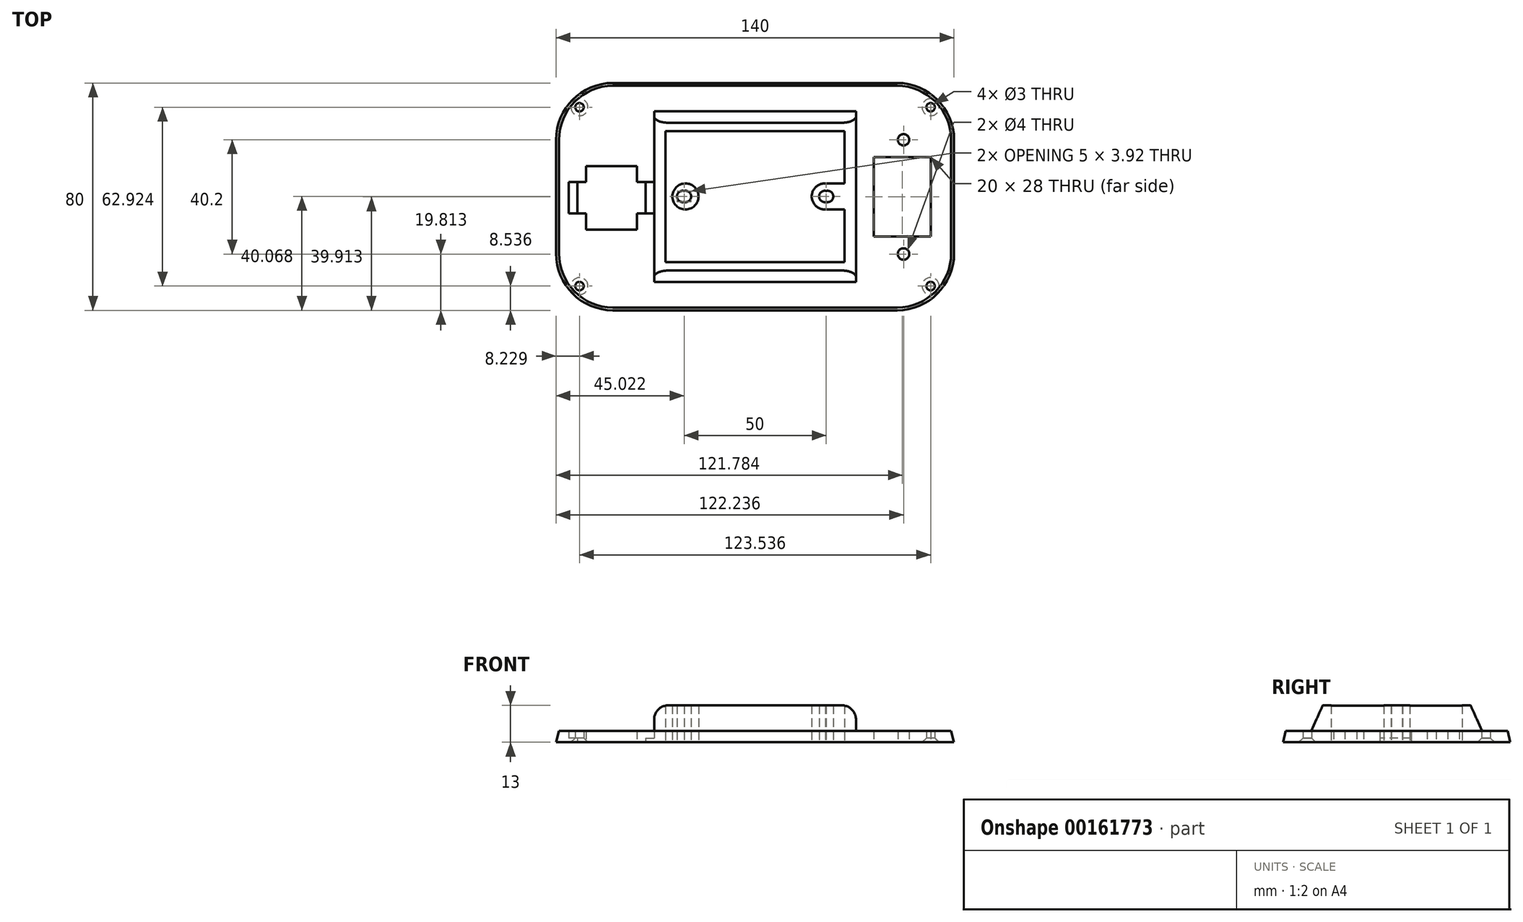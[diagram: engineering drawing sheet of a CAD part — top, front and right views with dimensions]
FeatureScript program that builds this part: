
annotation { "Feature Type Name" : "Feature", "Feature Type Description" : "" }
export const myFeature = defineFeature(function(context is Context, id is Id, definition is map)
    precondition{}
    {
        {
            var Q0;
            Q0=qCreatedBy(makeId("Top.planeOp"),FACE);
            var sketch = newSketch(context, id + "F0", { "sketchPlane" : qUnion([Q0])});
            skPoint(sketch, "E0.middle", {"position": v(7.13, 0.12) * mm});
            skLineSegment(sketch, "E1.bottom", {"start": v(38.63, 23.12) * mm, "end": v(-24.37, 23.12) * mm});
            skLineSegment(sketch, "E1.top", {"start": v(38.63, -22.88) * mm, "end": v(-24.37, -22.88) * mm});
            skLineSegment(sketch, "E1.left", {"start": v(38.63, 23.12) * mm, "end": v(38.63, -22.88) * mm});
            skLineSegment(sketch, "E1.right", {"start": v(-24.37, 23.12) * mm, "end": v(-24.37, -22.88) * mm});
            skCircle(sketch, "E2", {"center": v(31.65, 0.19) * mm, "radius": 2 * mm});
            skPoint(sketch, "E3.middle", {"position": v(32.65, 0.19) * mm});
            skPoint(sketch, "E4.middle", {"position": v(-18.35, 0.19) * mm});
            skCircle(sketch, "E5", {"center": v(-17.35, 0.19) * mm, "radius": 2 * mm});
            skCircle(sketch, "E6", {"center": v(59.37, 20.13) * mm, "radius": 2 * mm});
            skCircle(sketch, "E7", {"center": v(59.37, -20.07) * mm, "radius": 2 * mm});
            skPoint(sketch, "E8.middle", {"position": v(58.91, 0.03) * mm});
            skPoint(sketch, "E9.visualSharp", {"position": v(-62.87, 30.12) * mm});
            skPoint(sketch, "E10.visualSharp", {"position": v(77.13, 30.12) * mm});
            skPoint(sketch, "E11.visualSharp", {"position": v(77.13, -29.88) * mm});
            skPoint(sketch, "E12.visualSharp", {"position": v(-62.87, -29.88) * mm});
            skLineSegment(sketch, "E13.bottom", {"start": v(-34.39, -11.43) * mm, "end": v(-52.39, -11.43) * mm});
            skLineSegment(sketch, "E13.top", {"start": v(-34.39, 10.87) * mm, "end": v(-52.39, 10.87) * mm});
            skLineSegment(sketch, "E13.left", {"start": v(-34.39, -11.43) * mm, "end": v(-34.39, 10.87) * mm});
            skLineSegment(sketch, "E13.right", {"start": v(-52.39, -11.43) * mm, "end": v(-52.39, 10.87) * mm});
            skPoint(sketch, "E13.middle", {"position": v(-43.39, -0.28) * mm});
            skLineSegment(sketch, "E14.bottom", {"start": v(-55.39, 5.22) * mm, "end": v(-31.39, 5.22) * mm});
            skLineSegment(sketch, "E14.top", {"start": v(-55.39, -5.78) * mm, "end": v(-31.39, -5.78) * mm});
            skLineSegment(sketch, "E14.left", {"start": v(-55.39, 5.22) * mm, "end": v(-55.39, -5.78) * mm});
            skLineSegment(sketch, "E14.right", {"start": v(-31.39, 5.22) * mm, "end": v(-31.39, -5.78) * mm});
            skLineSegment(sketch, "E15.bottom", {"start": v(-28.39, 30.12) * mm, "end": v(42.64, 30.12) * mm});
            skLineSegment(sketch, "E15.top", {"start": v(-28.39, -29.88) * mm, "end": v(42.64, -29.88) * mm});
            skLineSegment(sketch, "E15.left", {"start": v(-28.39, 30.12) * mm, "end": v(-28.39, -29.88) * mm});
            skLineSegment(sketch, "E15.right", {"start": v(42.64, 30.12) * mm, "end": v(42.64, -29.88) * mm});
            skLineSegment(sketch, "E16.bottom", {"start": v(-31.39, 5.22) * mm, "end": v(-28.39, 5.22) * mm});
            skLineSegment(sketch, "E16.top", {"start": v(-31.39, -5.78) * mm, "end": v(-28.39, -5.78) * mm});
            skLineSegment(sketch, "E16.right", {"start": v(-28.39, 5.22) * mm, "end": v(-28.39, -5.78) * mm});
            skLineSegment(sketch, "E17.bottom", {"start": v(-55.39, 5.22) * mm, "end": v(-58.39, 5.22) * mm});
            skLineSegment(sketch, "E17.top", {"start": v(-55.39, -5.78) * mm, "end": v(-58.39, -5.78) * mm});
            skLineSegment(sketch, "E17.right", {"start": v(-58.39, 5.22) * mm, "end": v(-58.39, -5.78) * mm});
            skLineSegment(sketch, "E18.bottom", {"start": v(57.13, 40.12) * mm, "end": v(-42.87, 40.12) * mm});
            skLineSegment(sketch, "E18.top", {"start": v(57.13, -39.88) * mm, "end": v(-42.87, -39.88) * mm});
            skLineSegment(sketch, "E18.left", {"start": v(77.13, 20.12) * mm, "end": v(77.13, -19.88) * mm});
            skLineSegment(sketch, "E18.right", {"start": v(-62.87, 20.12) * mm, "end": v(-62.87, -19.88) * mm});
            skPoint(sketch, "E19.visualSharp", {"position": v(-62.87, 40.12) * mm});
            skArc(sketch, "E19.filletArc", {"start": v(-42.87, 40.12) * mm, "mid": v(-57.01, 34.26) * mm, "end": v(-62.87, 20.12) * mm});
            skPoint(sketch, "E20.visualSharp", {"position": v(77.13, 40.12) * mm});
            skArc(sketch, "E20.filletArc", {"start": v(77.13, 20.12) * mm, "mid": v(71.27, 34.26) * mm, "end": v(57.13, 40.12) * mm});
            skPoint(sketch, "E21.visualSharp", {"position": v(77.13, -39.88) * mm});
            skArc(sketch, "E21.filletArc", {"start": v(57.13, -39.88) * mm, "mid": v(71.27, -34.02) * mm, "end": v(77.13, -19.88) * mm});
            skPoint(sketch, "E22.visualSharp", {"position": v(-62.87, -39.88) * mm});
            skArc(sketch, "E22.filletArc", {"start": v(-62.87, -19.88) * mm, "mid": v(-57.01, -34.02) * mm, "end": v(-42.87, -39.88) * mm});
            skLineSegment(sketch, "E23.bottom", {"start": v(-42.87, 44.12) * mm, "end": v(57.13, 44.12) * mm});
            skLineSegment(sketch, "E23.top", {"start": v(-42.87, -43.88) * mm, "end": v(57.13, -43.88) * mm});
            skLineSegment(sketch, "E23.left", {"start": v(-66.87, 20.12) * mm, "end": v(-66.87, -19.88) * mm});
            skLineSegment(sketch, "E23.right", {"start": v(81.13, 20.12) * mm, "end": v(81.13, -19.88) * mm});
            skPoint(sketch, "E24.visualSharp", {"position": v(-66.87, 44.12) * mm});
            skArc(sketch, "E24.filletArc", {"start": v(-42.87, 44.12) * mm, "mid": v(-59.84, 37.09) * mm, "end": v(-66.87, 20.12) * mm});
            skPoint(sketch, "E25.visualSharp", {"position": v(81.13, 44.12) * mm});
            skArc(sketch, "E25.filletArc", {"start": v(81.13, 20.12) * mm, "mid": v(74.1, 37.09) * mm, "end": v(57.13, 44.12) * mm});
            skPoint(sketch, "E26.visualSharp", {"position": v(81.13, -43.88) * mm});
            skArc(sketch, "E26.filletArc", {"start": v(57.13, -43.88) * mm, "mid": v(74.1, -36.85) * mm, "end": v(81.13, -19.88) * mm});
            skPoint(sketch, "E27.visualSharp", {"position": v(-66.87, -43.88) * mm});
            skArc(sketch, "E27.filletArc", {"start": v(-66.87, -19.88) * mm, "mid": v(-59.84, -36.85) * mm, "end": v(-42.87, -43.88) * mm});
            skCircle(sketch, "E28", {"center": v(68.9, 31.58) * mm, "radius": 3.5 * mm});
            skCircle(sketch, "E29", {"center": v(68.9, 31.58) * mm, "radius": 1.5 * mm});
            skCircle(sketch, "E30", {"center": v(-54.64, 31.58) * mm, "radius": 3.5 * mm});
            skCircle(sketch, "E31", {"center": v(-54.64, 31.58) * mm, "radius": 1.5 * mm});
            skCircle(sketch, "E32", {"center": v(-54.64, -31.34) * mm, "radius": 3.5 * mm});
            skCircle(sketch, "E33", {"center": v(-54.64, -31.34) * mm, "radius": 1.5 * mm});
            skCircle(sketch, "E34", {"center": v(68.9, -31.34) * mm, "radius": 3.5 * mm});
            skCircle(sketch, "E35", {"center": v(68.9, -31.34) * mm, "radius": 1.5 * mm});
            skLineSegment(sketch, "E36.right", {"start": v(-24.37, 4.8) * mm, "end": v(-24.37, -4.4) * mm});
            skCircle(sketch, "E37", {"center": v(-17.35, 0.19) * mm, "radius": 4.6 * mm});
            skCircle(sketch, "E38", {"center": v(31.65, 0.19) * mm, "radius": 4.59 * mm});
            skLineSegment(sketch, "E39", {"start": v(31.92, 4.77) * mm, "end": v(38.65, 4.8) * mm});
            skLineSegment(sketch, "E40", {"start": v(31.64, -4.4) * mm, "end": v(38.65, -4.43) * mm});
            skLineSegment(sketch, "E41", {"start": v(-17.31, -4.4) * mm, "end": v(-24.37, -4.4) * mm});
            skLineSegment(sketch, "E42", {"start": v(-17.51, 4.78) * mm, "end": v(-24.37, 4.8) * mm});
            skLineSegment(sketch, "E43.bottom", {"start": v(68.91, 14.03) * mm, "end": v(48.91, 14.03) * mm});
            skLineSegment(sketch, "E43.top", {"start": v(68.91, -13.97) * mm, "end": v(48.91, -13.97) * mm});
            skLineSegment(sketch, "E43.left", {"start": v(68.91, 14.03) * mm, "end": v(68.91, -13.97) * mm});
            skLineSegment(sketch, "E43.right", {"start": v(48.91, 14.03) * mm, "end": v(48.91, -13.97) * mm});
            skCircle(sketch, "E44", {"center": v(-18.35, 0.19) * mm, "radius": 2 * mm});
            skCircle(sketch, "E45", {"center": v(32.65, 0.19) * mm, "radius": 2 * mm});
            skSolve(sketch);
        }
        {
            var Q0;
            Q0=makeQuery(id+"F0.imprint","IMPRINT",FACE,{"disambiguationData":[TD([[makeQuery(id+"F0.imprint","IMPRINT",EDGE,{"derivedFrom":sQuery(id+"F0.wireOp",EDGE,"E6")}),-1.0]])]});
            var Q1;
            Q1=makeQuery(id+"F0.imprint","IMPRINT",FACE,{"disambiguationData":[TD([[makeQuery(id+"F0.imprint","IMPRINT",EDGE,{"derivedFrom":sQuery(id+"F0.wireOp",EDGE,"E28")}),1.0]])]});
            var Q2;
            Q2=makeQuery(id+"F0.imprint","IMPRINT",FACE,{"disambiguationData":[TD([[makeQuery(id+"F0.imprint","IMPRINT",EDGE,{"derivedFrom":sQuery(id+"F0.wireOp",EDGE,"E32")}),1.0]])]});
            var Q3;
            Q3=makeQuery(id+"F0.imprint","IMPRINT",FACE,{"disambiguationData":[TD([[makeQuery(id+"F0.imprint","IMPRINT",EDGE,{"derivedFrom":sQuery(id+"F0.wireOp",EDGE,"E34")}),1.0]])]});
            var Q4;
            {var subQ1=sQuery(id+"F0.wireOp",EDGE,"E4.bottom");Q4=makeQuery(id+"F0.imprint","IMPRINT",FACE,{"disambiguationData":[TD([[makeQuery(id+"F0.imprint","IMPRINT",EDGE,{"derivedFrom":subQ1}),1.0]])]});}
            var Q5;
            Q5=makeQuery(id+"F0.imprint","IMPRINT",FACE,{"disambiguationData":[TD([[makeQuery(id+"F0.imprint","IMPRINT",EDGE,{"derivedFrom":sQuery(id+"F0.wireOp",EDGE,"E30")}),1.0]])]});
            extrude(context, id + "F1", {"entities" : qUnion([Q0, Q1, Q2, Q3, Q4, Q5]), "depth" : 4 * mm});
        }
        {
            var Q0;
            Q0=makeQuery(id+"F0.imprint","IMPRINT",FACE,{"disambiguationData":[TD([[makeQuery(id+"F0.imprint","IMPRINT",EDGE,{"derivedFrom":sQuery(id+"F0.wireOp",EDGE,"E16.bottom")}),-1.0]])]});
            var Q1;
            Q1=makeQuery(id+"F0.imprint","IMPRINT",FACE,{"disambiguationData":[TD([[makeQuery(id+"F0.imprint","IMPRINT",EDGE,{"derivedFrom":sQuery(id+"F0.wireOp",EDGE,"E17.bottom")}),1.0]])]});
            extrude(context, id + "F2", {"entities" : qUnion([Q0, Q1]), "operationType" : NewBodyOperationType.ADD, "depth" : 1.5 * mm});
        }
        {
            var Q0;
            {var subQ6=sQuery(id+"F0.wireOp",EDGE,"E1.bottom");Q0=makeQuery(id+"F0.imprint","IMPRINT",FACE,{"disambiguationData":[TD([[makeQuery(id+"F0.imprint","IMPRINT",EDGE,{"derivedFrom":subQ6}),-1.0]])]});}
            var Q1;
            {var subQ0=sQuery(id+"F0.wireOp",EDGE,"E36.right");Q1=makeQuery(id+"F0.imprint","IMPRINT",FACE,{"disambiguationData":[TD([[makeQuery(id+"F0.imprint","IMPRINT",EDGE,{"derivedFrom":subQ0}),1.0]])]});}
            var Q2;
            {var subQ0=sQuery(id+"F0.wireOp",EDGE,"E39");var subQ1=sQuery(id+"F0.wireOp",EDGE,"E1.left");var subQ2=makeQuery(id+"F0.imprint","INTERSECT",VERTEX,{"derivedFrom":[subQ1,subQ0]});Q2=makeQuery(id+"F0.imprint","IMPRINT",FACE,{"disambiguationData":[TD([[makeQuery(id+"F0.imprint","IMPRINT",EDGE,{"disambiguationData":[TD([[subQ2,-1.0]])],"derivedFrom":subQ1}),-1.0]])]});}
            var Q3;
            {var subQ5=sQuery(id+"F0.wireOp",EDGE,"E44");var subQ6=sQuery(id+"F0.wireOp",EDGE,"E5");var subQ7=makeQuery(id+"F0.imprint","INTERSECT",VERTEX,{"disambiguationData":[OD(0.0)],"derivedFrom":[subQ6,subQ5]});Q3=makeQuery(id+"F0.imprint","IMPRINT",FACE,{"disambiguationData":[TD([[makeQuery(id+"F0.imprint","IMPRINT",EDGE,{"disambiguationData":[TD([[subQ7,-1.0]])],"derivedFrom":subQ6}),-1.0]])]});}
            var Q4;
            {var subQ0=sQuery(id+"F0.wireOp",EDGE,"E45");var subQ1=sQuery(id+"F0.wireOp",EDGE,"E2");var subQ2=makeQuery(id+"F0.imprint","INTERSECT",VERTEX,{"disambiguationData":[OD(0.0)],"derivedFrom":[subQ1,subQ0]});Q4=makeQuery(id+"F0.imprint","IMPRINT",FACE,{"disambiguationData":[TD([[makeQuery(id+"F0.imprint","IMPRINT",EDGE,{"disambiguationData":[TD([[subQ2,1.0]])],"derivedFrom":subQ1}),-1.0]])]});}
            extrude(context, id + "F3", {"entities" : qUnion([Q0, Q1, Q2, Q3, Q4]), "operationType" : NewBodyOperationType.ADD, "depth" : 13 * mm});
        }
        {
            var Q0;
            Q0=makeQuery(id+"F3.opExtrude","CAP_EDGE",EDGE,{"disambiguationData":[OSD([sQuery(id+"F0.wireOp",EDGE,"E15.top")])],"isStart":false});
            var Q1;
            Q1=makeQuery(id+"F3.opExtrude","CAP_EDGE",EDGE,{"disambiguationData":[OSD([sQuery(id+"F0.wireOp",EDGE,"E15.bottom")])],"isStart":false});
            chamfer(context, id + "F4", {"entities" : qUnion([Q0, Q1]), "chamferType" : ChamferType.TWO_OFFSETS, "width1" : 4 * mm, "oppositeDirection" : false, "width2" : 9 * mm, "tangentPropagation" : true});
        }
        {
            var Q0;
            Q0=makeQuery(id+"F1.opExtrude","CAP_EDGE",EDGE,{"disambiguationData":[OSD([sQuery(id+"F0.wireOp",EDGE,"E19.filletArc")])],"isStart":false});
            chamfer(context, id + "F5", {"entities" : qUnion([Q0]), "chamferType" : ChamferType.TWO_OFFSETS, "width1" : 1 * mm, "oppositeDirection" : false, "width2" : 4 * mm, "tangentPropagation" : true});
        }
        {
            var Q0;
            Q0=makeQuery(id+"F1.opExtrude","CAP_EDGE",EDGE,{"disambiguationData":[OSD([sQuery(id+"F0.wireOp",EDGE,"E31")])],"isStart":true});
            var Q1;
            Q1=makeQuery(id+"F1.opExtrude","CAP_EDGE",EDGE,{"disambiguationData":[OSD([sQuery(id+"F0.wireOp",EDGE,"E29")])],"isStart":true});
            var Q2;
            Q2=makeQuery(id+"F1.opExtrude","CAP_EDGE",EDGE,{"disambiguationData":[OSD([sQuery(id+"F0.wireOp",EDGE,"E35")])],"isStart":true});
            var Q3;
            Q3=makeQuery(id+"F1.opExtrude","CAP_EDGE",EDGE,{"disambiguationData":[OSD([sQuery(id+"F0.wireOp",EDGE,"E33")])],"isStart":true});
            chamfer(context, id + "F6", {"entities" : qUnion([Q0, Q1, Q2, Q3]), "width" : 1.5 * mm, "tangentPropagation" : true});
        }
        {
            var Q0;
            Q0=makeQuery(id+"F3.opExtrude","CAP_EDGE",EDGE,{"disambiguationData":[OSD([sQuery(id+"F0.wireOp",EDGE,"E15.left"),sQuery(id+"F0.wireOp",EDGE,"E16.right")])],"isStart":false});
            var Q1;
            Q1=makeQuery(id+"F3.opExtrude","CAP_EDGE",EDGE,{"disambiguationData":[OSD([sQuery(id+"F0.wireOp",EDGE,"E15.right")])],"isStart":false});
            fillet(context, id + "F7", {"entities" : qUnion([Q0, Q1]), "radius" : 5 * mm, "tangentPropagation" : true, "allowEdgeOverflow" : false});
        }
    });
